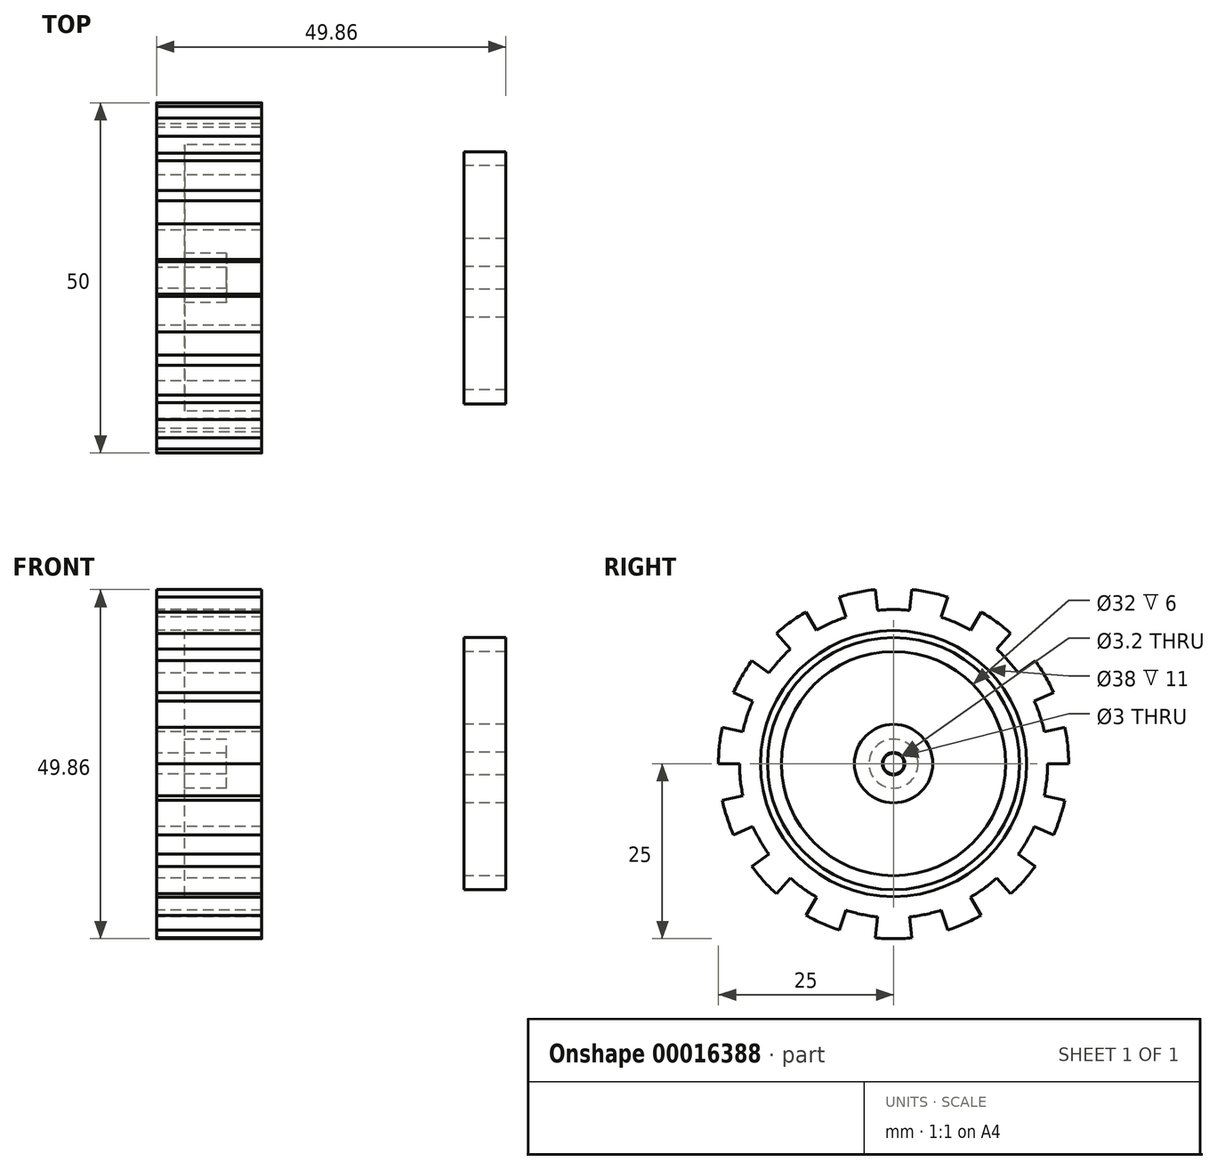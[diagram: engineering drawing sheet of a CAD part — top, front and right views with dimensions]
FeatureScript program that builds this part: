
annotation { "Feature Type Name" : "Feature", "Feature Type Description" : "" }
export const myFeature = defineFeature(function(context is Context, id is Id, definition is map)
    precondition{}
    {
        {
            var Q0;
            Q0=qCreatedBy(makeId("Right.planeOp"),FACE);
            var sketch = newSketch(context, id + "F0", { "sketchPlane" : qUnion([Q0])});
            skArc(sketch, "E0", {"start": v(-22, 0) * mm, "mid": v(-21.88, -2.3) * mm, "end": v(-21.52, -4.57) * mm});
            skArc(sketch, "E1", {"start": v(-12.5, 21.65) * mm, "mid": v(-14.7, 20.23) * mm, "end": v(-16.73, 18.58) * mm});
            skLineSegment(sketch, "E2", {"start": v(-25, 0) * mm, "end": v(-22, 0) * mm});
            skLineSegment(sketch, "E3.1.0", {"start": v(-24.45, -5.2) * mm, "end": v(-21.52, -4.57) * mm});
            skLineSegment(sketch, "E3.2.0", {"start": v(-22.84, -10.17) * mm, "end": v(-20.1, -8.95) * mm});
            skLineSegment(sketch, "E3.3.0", {"start": v(-20.23, -14.7) * mm, "end": v(-17.8, -12.93) * mm});
            skLineSegment(sketch, "E3.4.0", {"start": v(-16.73, -18.58) * mm, "end": v(-14.72, -16.35) * mm});
            skLineSegment(sketch, "E3.5.0", {"start": v(-12.5, -21.65) * mm, "end": v(-11, -19.05) * mm});
            skLineSegment(sketch, "E3.6.0", {"start": v(-7.73, -23.78) * mm, "end": v(-6.8, -20.92) * mm});
            skLineSegment(sketch, "E3.7.0", {"start": v(-2.61, -24.86) * mm, "end": v(-2.3, -21.88) * mm});
            skLineSegment(sketch, "E3.8.0", {"start": v(2.61, -24.86) * mm, "end": v(2.3, -21.88) * mm});
            skLineSegment(sketch, "E3.9.0", {"start": v(7.73, -23.78) * mm, "end": v(6.8, -20.92) * mm});
            skLineSegment(sketch, "E3.10.0", {"start": v(12.5, -21.65) * mm, "end": v(11, -19.05) * mm});
            skLineSegment(sketch, "E3.11.0", {"start": v(16.73, -18.58) * mm, "end": v(14.72, -16.35) * mm});
            skLineSegment(sketch, "E3.12.0", {"start": v(20.23, -14.7) * mm, "end": v(17.8, -12.93) * mm});
            skLineSegment(sketch, "E3.13.0", {"start": v(22.84, -10.17) * mm, "end": v(20.1, -8.95) * mm});
            skLineSegment(sketch, "E3.14.0", {"start": v(24.45, -5.2) * mm, "end": v(21.52, -4.57) * mm});
            skLineSegment(sketch, "E3.15.0", {"start": v(25, 0) * mm, "end": v(22, 0) * mm});
            skLineSegment(sketch, "E3.16.0", {"start": v(24.45, 5.2) * mm, "end": v(21.52, 4.57) * mm});
            skLineSegment(sketch, "E3.17.0", {"start": v(22.84, 10.17) * mm, "end": v(20.1, 8.95) * mm});
            skLineSegment(sketch, "E3.18.0", {"start": v(20.23, 14.7) * mm, "end": v(17.8, 12.93) * mm});
            skLineSegment(sketch, "E3.19.0", {"start": v(16.73, 18.58) * mm, "end": v(14.72, 16.35) * mm});
            skLineSegment(sketch, "E3.20.0", {"start": v(12.5, 21.65) * mm, "end": v(11, 19.05) * mm});
            skLineSegment(sketch, "E3.21.0", {"start": v(7.73, 23.78) * mm, "end": v(6.8, 20.92) * mm});
            skLineSegment(sketch, "E3.22.0", {"start": v(2.61, 24.86) * mm, "end": v(2.3, 21.88) * mm});
            skLineSegment(sketch, "E3.23.0", {"start": v(-2.61, 24.86) * mm, "end": v(-2.3, 21.88) * mm});
            skLineSegment(sketch, "E3.24.0", {"start": v(-7.73, 23.78) * mm, "end": v(-6.8, 20.92) * mm});
            skLineSegment(sketch, "E3.25.0", {"start": v(-12.5, 21.65) * mm, "end": v(-11, 19.05) * mm});
            skLineSegment(sketch, "E3.26.0", {"start": v(-16.73, 18.58) * mm, "end": v(-14.72, 16.35) * mm});
            skLineSegment(sketch, "E3.27.0", {"start": v(-20.23, 14.7) * mm, "end": v(-17.8, 12.93) * mm});
            skLineSegment(sketch, "E3.28.0", {"start": v(-22.84, 10.17) * mm, "end": v(-20.1, 8.95) * mm});
            skLineSegment(sketch, "E3.29.0", {"start": v(-24.45, 5.2) * mm, "end": v(-21.52, 4.57) * mm});
            skArc(sketch, "E4.trimOffspring", {"start": v(-20.1, 8.95) * mm, "mid": v(-20.92, 6.8) * mm, "end": v(-21.52, 4.57) * mm});
            skArc(sketch, "E5.trimOffspring", {"start": v(-14.72, 16.35) * mm, "mid": v(-16.35, 14.72) * mm, "end": v(-17.8, 12.93) * mm});
            skArc(sketch, "E6.trimOffspring", {"start": v(-6.8, 20.92) * mm, "mid": v(-8.95, 20.1) * mm, "end": v(-11, 19.05) * mm});
            skArc(sketch, "E7.trimOffspring", {"start": v(2.3, 21.88) * mm, "mid": v(0, 22) * mm, "end": v(-2.3, 21.88) * mm});
            skArc(sketch, "E8.trimOffspring", {"start": v(11, 19.05) * mm, "mid": v(8.95, 20.1) * mm, "end": v(6.8, 20.92) * mm});
            skArc(sketch, "E9.trimOffspring", {"start": v(17.8, 12.93) * mm, "mid": v(16.35, 14.72) * mm, "end": v(14.72, 16.35) * mm});
            skArc(sketch, "E10.trimOffspring", {"start": v(21.52, 4.57) * mm, "mid": v(20.92, 6.8) * mm, "end": v(20.1, 8.95) * mm});
            skArc(sketch, "E11.trimOffspring", {"start": v(21.52, -4.57) * mm, "mid": v(21.88, -2.3) * mm, "end": v(22, 0) * mm});
            skArc(sketch, "E12.trimOffspring", {"start": v(17.8, -12.93) * mm, "mid": v(19.05, -11) * mm, "end": v(20.1, -8.95) * mm});
            skArc(sketch, "E13.trimOffspring", {"start": v(11, -19.05) * mm, "mid": v(12.93, -17.8) * mm, "end": v(14.72, -16.35) * mm});
            skArc(sketch, "E14.trimOffspring", {"start": v(2.3, -21.88) * mm, "mid": v(4.57, -21.52) * mm, "end": v(6.8, -20.92) * mm});
            skArc(sketch, "E15.trimOffspring", {"start": v(-6.8, -20.92) * mm, "mid": v(-4.57, -21.52) * mm, "end": v(-2.3, -21.88) * mm});
            skArc(sketch, "E16.trimOffspring", {"start": v(-14.72, -16.35) * mm, "mid": v(-12.93, -17.8) * mm, "end": v(-11, -19.05) * mm});
            skArc(sketch, "E17.trimOffspring", {"start": v(-20.1, -8.95) * mm, "mid": v(-19.05, -11) * mm, "end": v(-17.8, -12.93) * mm});
            skArc(sketch, "E18.trimOffspring", {"start": v(-2.61, 24.86) * mm, "mid": v(-5.2, 24.45) * mm, "end": v(-7.73, 23.78) * mm});
            skArc(sketch, "E19.trimOffspring", {"start": v(7.73, 23.78) * mm, "mid": v(5.2, 24.45) * mm, "end": v(2.61, 24.86) * mm});
            skArc(sketch, "E20.trimOffspring", {"start": v(16.73, 18.58) * mm, "mid": v(14.7, 20.23) * mm, "end": v(12.5, 21.65) * mm});
            skArc(sketch, "E21.trimOffspring", {"start": v(22.84, 10.17) * mm, "mid": v(21.65, 12.5) * mm, "end": v(20.23, 14.7) * mm});
            skArc(sketch, "E22.trimOffspring", {"start": v(25, 0) * mm, "mid": v(24.86, 2.61) * mm, "end": v(24.45, 5.2) * mm});
            skArc(sketch, "E23.trimOffspring", {"start": v(22.84, -10.17) * mm, "mid": v(23.78, -7.73) * mm, "end": v(24.45, -5.2) * mm});
            skArc(sketch, "E24.trimOffspring", {"start": v(16.73, -18.58) * mm, "mid": v(18.58, -16.73) * mm, "end": v(20.23, -14.7) * mm});
            skArc(sketch, "E25.trimOffspring", {"start": v(7.73, -23.78) * mm, "mid": v(10.17, -22.84) * mm, "end": v(12.5, -21.65) * mm});
            skArc(sketch, "E26.trimOffspring", {"start": v(-2.61, -24.86) * mm, "mid": v(0, -25) * mm, "end": v(2.61, -24.86) * mm});
            skArc(sketch, "E27.trimOffspring", {"start": v(-12.5, -21.65) * mm, "mid": v(-10.17, -22.84) * mm, "end": v(-7.73, -23.78) * mm});
            skArc(sketch, "E28.trimOffspring", {"start": v(-20.23, -14.7) * mm, "mid": v(-18.58, -16.73) * mm, "end": v(-16.73, -18.58) * mm});
            skArc(sketch, "E29.trimOffspring", {"start": v(-24.45, -5.2) * mm, "mid": v(-23.78, -7.73) * mm, "end": v(-22.84, -10.17) * mm});
            skArc(sketch, "E30.trimOffspring", {"start": v(-24.45, 5.2) * mm, "mid": v(-24.86, 2.61) * mm, "end": v(-25, 0) * mm});
            skArc(sketch, "E31.trimOffspring", {"start": v(-20.23, 14.7) * mm, "mid": v(-21.65, 12.5) * mm, "end": v(-22.84, 10.17) * mm});
            skCircle(sketch, "E32", {"center": v(0, 0) * mm, "radius": 19 * mm});
            skCircle(sketch, "E33", {"center": v(0, 0) * mm, "radius": 3.5 * mm});
            skCircle(sketch, "E34", {"center": v(0, 0) * mm, "radius": 1.5 * mm});
            skSolve(sketch);
        }
        {
            var Q0;
            Q0=makeQuery(id+"F0.imprint","IMPRINT",FACE,{"disambiguationData":[TD([[makeQuery(id+"F0.imprint","IMPRINT",EDGE,{"derivedFrom":sQuery(id+"F0.wireOp",EDGE,"E0")}),1.0]])]});
            extrude(context, id + "F1", {"entities" : qUnion([Q0]), "depth" : 15 * mm});
        }
        {
            var Q0;
            Q0=makeQuery(id+"F0.imprint","IMPRINT",FACE,{"disambiguationData":[TD([[makeQuery(id+"F0.imprint","IMPRINT",EDGE,{"derivedFrom":sQuery(id+"F0.wireOp",EDGE,"E32")}),1.0]])]});
            extrude(context, id + "F2", {"entities" : qUnion([Q0]), "operationType" : NewBodyOperationType.ADD, "depth" : 4 * mm});
        }
        {
            var Q0;
            Q0=makeQuery(id+"F0.imprint","IMPRINT",FACE,{"disambiguationData":[TD([[makeQuery(id+"F0.imprint","IMPRINT",EDGE,{"derivedFrom":sQuery(id+"F0.wireOp",EDGE,"E33")}),1.0]])]});
            extrude(context, id + "F3", {"entities" : qUnion([Q0]), "operationType" : NewBodyOperationType.ADD, "depth" : 10 * mm});
        }
        {
            var Q0;
            Q0=qCreatedBy(makeId("Front.planeOp"),FACE);
            var sketch = newSketch(context, id + "F4", { "sketchPlane" : qUnion([Q0])});
            skLineSegment(sketch, "E35.bottom", {"start": v(43.86, 5.6) * mm, "end": v(49.86, 5.6) * mm});
            skLineSegment(sketch, "E35.top", {"start": v(43.86, 1.6) * mm, "end": v(49.86, 1.6) * mm});
            skLineSegment(sketch, "E35.left", {"start": v(43.86, 5.6) * mm, "end": v(43.86, 1.6) * mm});
            skLineSegment(sketch, "E35.right", {"start": v(49.86, 5.6) * mm, "end": v(49.86, 1.6) * mm});
            skLineSegment(sketch, "E36.bottom", {"start": v(43.86, 5.6) * mm, "end": v(45.86, 5.6) * mm});
            skLineSegment(sketch, "E36.top", {"start": v(43.86, 16) * mm, "end": v(45.86, 16) * mm});
            skLineSegment(sketch, "E36.left", {"start": v(43.86, 5.6) * mm, "end": v(43.86, 16) * mm});
            skLineSegment(sketch, "E36.right", {"start": v(45.86, 5.6) * mm, "end": v(45.86, 16) * mm});
            skLineSegment(sketch, "E37.bottom", {"start": v(43.86, 18) * mm, "end": v(49.86, 18) * mm});
            skLineSegment(sketch, "E37.top", {"start": v(43.86, 16) * mm, "end": v(49.86, 16) * mm});
            skLineSegment(sketch, "E37.left", {"start": v(43.86, 18) * mm, "end": v(43.86, 16) * mm});
            skLineSegment(sketch, "E37.right", {"start": v(49.86, 18) * mm, "end": v(49.86, 16) * mm});
            skLineSegment(sketch, "E38", {"start": v(35.66, 0) * mm, "end": v(64.6, 0) * mm, "construction": true});
            skSolve(sketch);
        }
        {
            var Q0;
            Q0=makeQuery(id+"F4.imprint","IMPRINT",FACE,{"disambiguationData":[TD([[makeQuery(id+"F4.imprint","IMPRINT",EDGE,{"derivedFrom":sQuery(id+"F4.wireOp",EDGE,"E37.bottom")}),-1.0]])]});
            var Q1;
            Q1=makeQuery(id+"F4.imprint","IMPRINT",FACE,{"disambiguationData":[TD([[makeQuery(id+"F4.imprint","IMPRINT",EDGE,{"derivedFrom":sQuery(id+"F4.wireOp",EDGE,"E36.bottom")}),1.0]])]});
            var Q2;
            Q2=makeQuery(id+"F4.imprint","IMPRINT",FACE,{"disambiguationData":[TD([[makeQuery(id+"F4.imprint","IMPRINT",EDGE,{"derivedFrom":sQuery(id+"F4.wireOp",EDGE,"E35.bottom")}),-1.0]])]});
            var Q3;
            Q3=sQuery(id+"F4.wireOp",EDGE,"E38");
            revolve(context, id + "F5", {"entities" : qUnion([Q0, Q1, Q2]), "axis" : qUnion([Q3]), "revolveType" : RevolveType.FULL});
        }
    });
